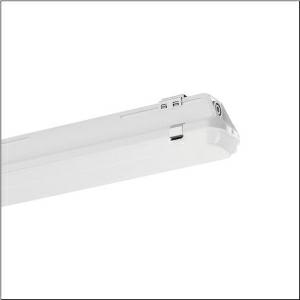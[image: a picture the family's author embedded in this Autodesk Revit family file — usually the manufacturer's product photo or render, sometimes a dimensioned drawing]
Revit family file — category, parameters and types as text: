
# Revit family: monsun_r__12_51fp30dp460h_c905
name_source: partatom
category: Lighting Fixtures
units: mm (PartAtom-declared; Revit-internal decimal feet)

## family parameters
Cut with Voids When Loaded = No
Host = Face
Light Source = No
Part Type = Normal
Room Calculation Point = No
Round Connector Dimension = Use Diameter
Shared = No

## types (1)
- --- (1 x LED, 5730 lm, 34.6 W, 4000K)
    Apparent Load = 35 VA
    CIE Flux Codes = 48 77 93 95 100
    Color Rendering = 80
    Color Temperature = 4000K
    Default Elevation = 1800 mm
    Description = Monsun® 12, damp-proof luminaire, chain hanger, primary optical cover: enclosure, of PA, light emission: direct distribution, primary light characteristic: symmetric, installation type: suspended mounting, surface-mounted, horizontal mounting, vertical mounting, LED rated luminous flux: 5.730 lm, light colour: 840, colour temperature: 4000K, control gear: ECG DALI, with terminal, 5-pole, max. 2.5mm², mains connection: 220..240V, AC, 50/60Hz, rated input power: 35W, luminaire housing, of glass-fibre reinforced polyester, uncoated, bright grey, length: 1.590 mm, width: 90 mm, height: 88mm, clip for enclosure, of stainless steel (V2A), ceiling mounting element, of stainless steel (V2A), chain hanger, of stainless steel (V2A), protection rating (complete): IP66, insulation class (complete): insulation class I (protective earthing), certification: CE, ENEC, VDE, protection symbol: D, impact resistance: IK08, permissible ambient temperature for indoor applications: -25..+40°C, standard: EN 50419, EN 60598-2-1, no direct snow, no direct sun, no direct rain, for indoor or canopied outdoor use, corresponds to IFS (International Featured Standards) requirements for safety and quality in the food industry, packaging unit: 1 piece
    Height = 89 mm
    Lamp = 1 x LED
    Lamp Light Flux = 5730 lm
    Lamp Power = 34.6 W
    Lamp count = 1
    Length = 1590 mm
    Luminous efficacy = 166 lm/W
    Manufacturer = Siteco
    ModVariant = No
    Model = 51FP30DP460H
    Mounting Place = Ceiling
    Mounting Type = Pendant
    Number of Poles = 1
    OnlyDefault = Yes
    Power Factor = 1
    Product Name = Monsun® 12
    Product group = damp-proof luminaire | ceiling pendant
    ProductGroupID = 908
    Protection Class = Protection class I
    Protection Degree = IP 66
    RLX_Detail_Level = 1
    RlxData = <blob elided: 92233 chars, md5=24894ab2>
    Socket = socket
    Standby Power = 0 W
    System Light Flux = 5730 lm
    System Power = 35 W
    Type Comments = factory setting: luminous flux: 100 % | dim-lin: 254 | 232 mA
    Type Image = l_1004748.jpg
    URL = http://relux.com
    VarID = @adj_136113
    Voltage = 0 V
    Weight = 0.00 kg
    Width = 90 mm

## geometry (parser evidence)
native form markers: Blend x4, Sweep x13
no freeform markers — native parametric forms only
